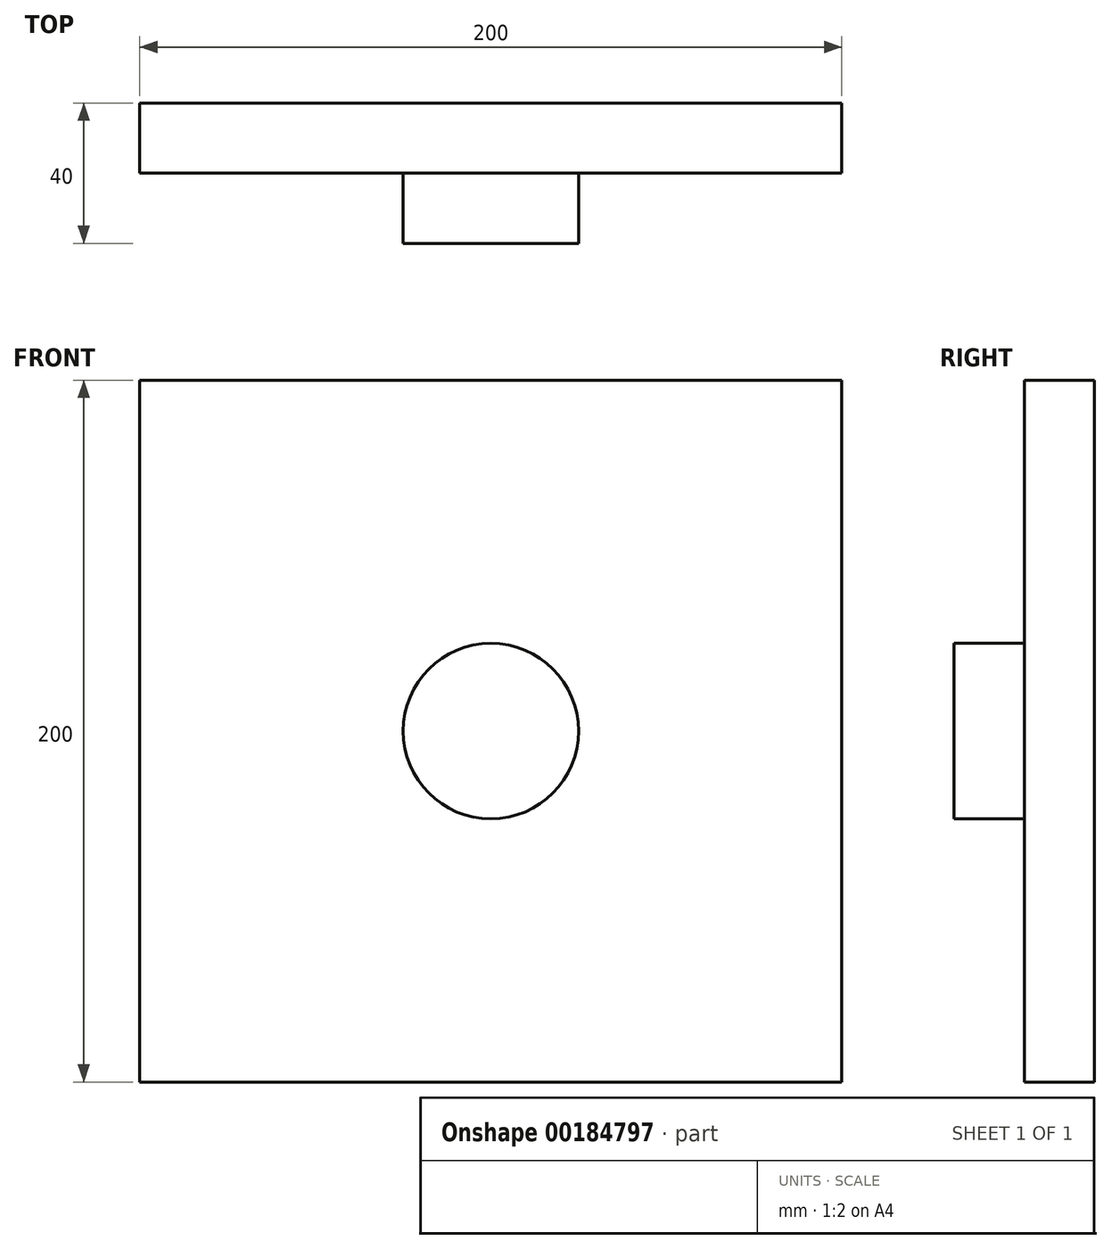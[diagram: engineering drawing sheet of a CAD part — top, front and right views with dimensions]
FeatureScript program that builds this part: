
annotation { "Feature Type Name" : "Feature", "Feature Type Description" : "" }
export const myFeature = defineFeature(function(context is Context, id is Id, definition is map)
    precondition{}
    {
        {
            var Q0;
            Q0=qCreatedBy(makeId("Front.planeOp"),FACE);
            var sketch = newSketch(context, id + "F0", { "sketchPlane" : qUnion([Q0])});
            skLineSegment(sketch, "E0.bottom", {"start": v(0, 0) * mm, "end": v(200, 0) * mm});
            skLineSegment(sketch, "E0.top", {"start": v(0, 200) * mm, "end": v(200, 200) * mm});
            skLineSegment(sketch, "E0.left", {"start": v(0, 0) * mm, "end": v(0, 200) * mm});
            skLineSegment(sketch, "E0.right", {"start": v(200, 0) * mm, "end": v(200, 200) * mm});
            skSolve(sketch);
        }
        {
            var Q0;
            Q0 = qSketchRegion(id + "F0", true);
            extrude(context, id + "F1", {"entities" : qUnion([Q0]), "depth" : 20 * mm});
        }
        {
            var Q0;
            Q0=makeQuery(id+"F1.opExtrude","CAP_FACE",FACE,{"disambiguationData":[OSD([sQuery(id+"F0.wireOp",EDGE,"E0.bottom"),sQuery(id+"F0.wireOp",EDGE,"E0.top"),sQuery(id+"F0.wireOp",EDGE,"E0.left"),sQuery(id+"F0.wireOp",EDGE,"E0.right")])],"isStart":false});
            var sketch = newSketch(context, id + "F2", { "sketchPlane" : qUnion([Q0])});
            skLineSegment(sketch, "E1", {"start": v(0, 100) * mm, "end": v(200, 100) * mm, "construction": true});
            skLineSegment(sketch, "E2", {"start": v(100, 0) * mm, "end": v(100, 200) * mm, "construction": true});
            skCircle(sketch, "E3", {"center": v(100, 100) * mm, "radius": 25 * mm});
            skSolve(sketch);
        }
        {
            var Q0;
            Q0=makeQuery(id+"F2.imprint","IMPRINT",FACE,{"disambiguationData":[TD([[makeQuery(id+"F2.imprint","IMPRINT",EDGE,{"derivedFrom":sQuery(id+"F2.wireOp",EDGE,"E3")}),1.0]])]});
            var Q1;
            Q1=sQuery(id+"F2.wireOp",EDGE,"E3");
            extrude(context, id + "F3", {"entities" : qUnion([Q0]), "surfaceEntities" : qUnion([Q1]), "depth" : 20 * mm});
        }
    });
